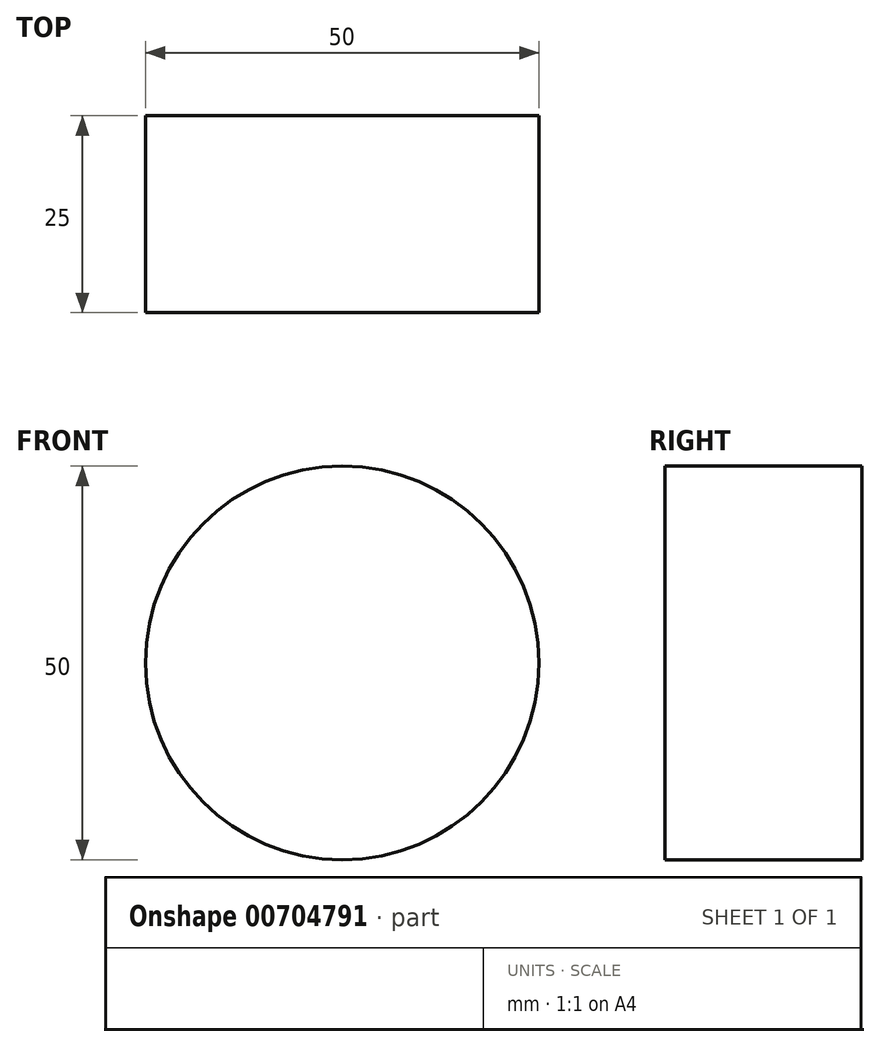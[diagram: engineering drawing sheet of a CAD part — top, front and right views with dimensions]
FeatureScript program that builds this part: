
annotation { "Feature Type Name" : "Feature", "Feature Type Description" : "" }
export const myFeature = defineFeature(function(context is Context, id is Id, definition is map)
    precondition{}
    {
        {
            var Q0;
            Q0=qCreatedBy(makeId("Front.planeOp"),FACE);
            var sketch = newSketch(context, id + "F0", { "sketchPlane" : qUnion([Q0])});
            skCircle(sketch, "E0", {"center": v(0, 0) * mm, "radius": 25 * mm});
            skSolve(sketch);
        }
        {
            var Q0;
            Q0 = qSketchRegion(id + "F0", true);
            extrude(context, id + "F1", {"entities" : qUnion([Q0]), "depth" : 25 * mm, "offsetDistance" : 25 * mm});
        }
    });
